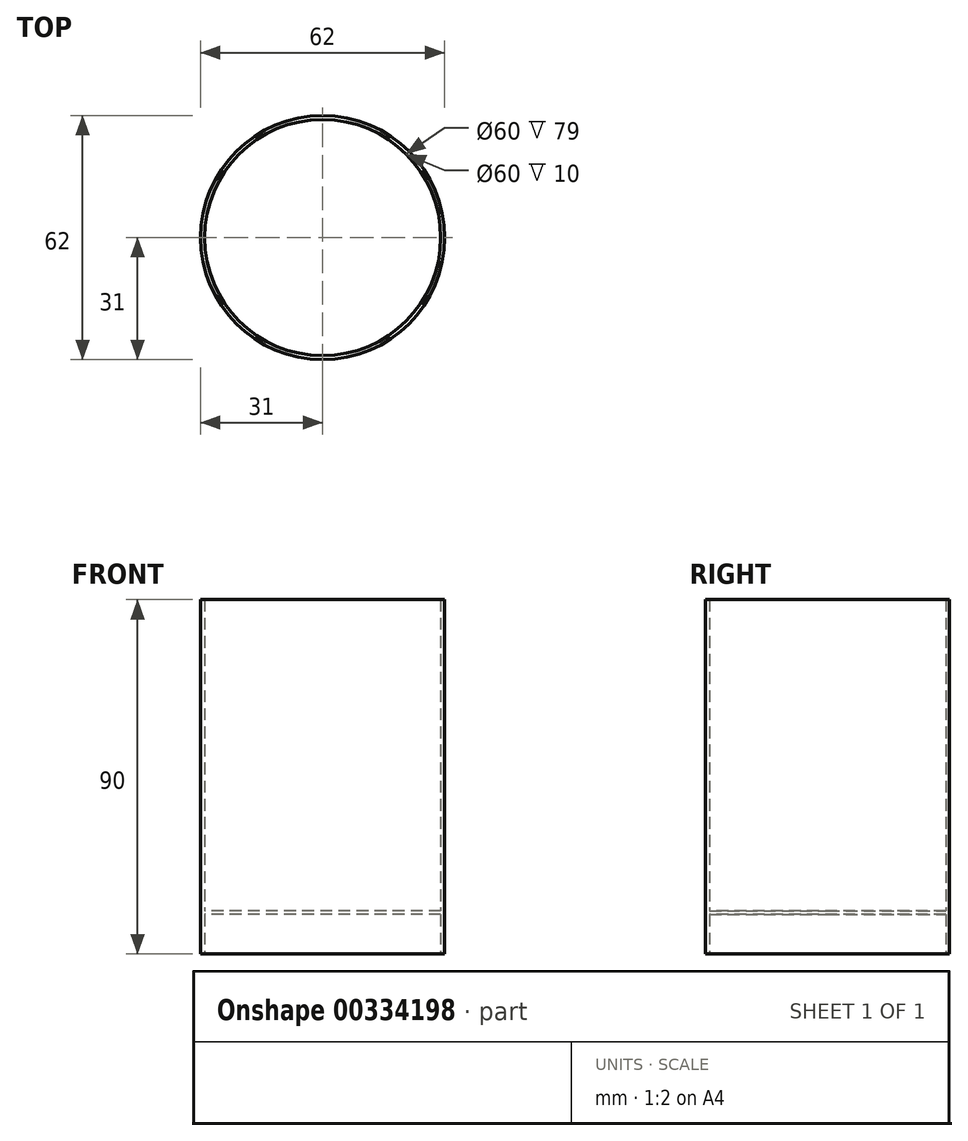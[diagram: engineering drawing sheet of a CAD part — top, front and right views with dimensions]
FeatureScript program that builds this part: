
annotation { "Feature Type Name" : "Feature", "Feature Type Description" : "" }
export const myFeature = defineFeature(function(context is Context, id is Id, definition is map)
    precondition{}
    {
        {
            var Q0;
            Q0=qCreatedBy(makeId("Top.planeOp"),FACE);
            var sketch = newSketch(context, id + "F0", { "sketchPlane" : qUnion([Q0])});
            skLineSegment(sketch, "E0", {"start": v(0, 0) * mm, "end": v(30, 0) * mm});
            skLineSegment(sketch, "E1", {"start": v(30, 0) * mm, "end": v(31, 0) * mm});
            skCircle(sketch, "E2", {"center": v(0, 0) * mm, "radius": 30 * mm});
            skCircle(sketch, "E3", {"center": v(0, 0) * mm, "radius": 31 * mm});
            skSolve(sketch);
        }
        {
            var Q0;
            Q0=makeQuery(id+"F0.imprint","IMPRINT",FACE,{"disambiguationData":[TD([[makeQuery(id+"F0.imprint","IMPRINT",EDGE,{"derivedFrom":sQuery(id+"F0.wireOp",EDGE,"E2")}),-1.0]])]});
            extrude(context, id + "F1", {"entities" : qUnion([Q0]), "depth" : 90 * mm});
        }
        {
            var Q0;
            Q0=makeQuery(id+"F0.imprint","IMPRINT",FACE,{"disambiguationData":[TD([[makeQuery(id+"F0.imprint","IMPRINT",EDGE,{"derivedFrom":sQuery(id+"F0.wireOp",EDGE,"E2")}),1.0]])]});
            extrude(context, id + "F2", {"entities" : qUnion([Q0]), "operationType" : NewBodyOperationType.ADD, "depth" : 11 * mm});
        }
        {
            var Q0;
            Q0=makeQuery(id+"F0.imprint","IMPRINT",FACE,{"disambiguationData":[TD([[makeQuery(id+"F0.imprint","IMPRINT",EDGE,{"derivedFrom":sQuery(id+"F0.wireOp",EDGE,"E2")}),1.0]])]});
            extrude(context, id + "F3", {"entities" : qUnion([Q0]), "operationType" : NewBodyOperationType.REMOVE, "depth" : 10 * mm});
        }
    });
